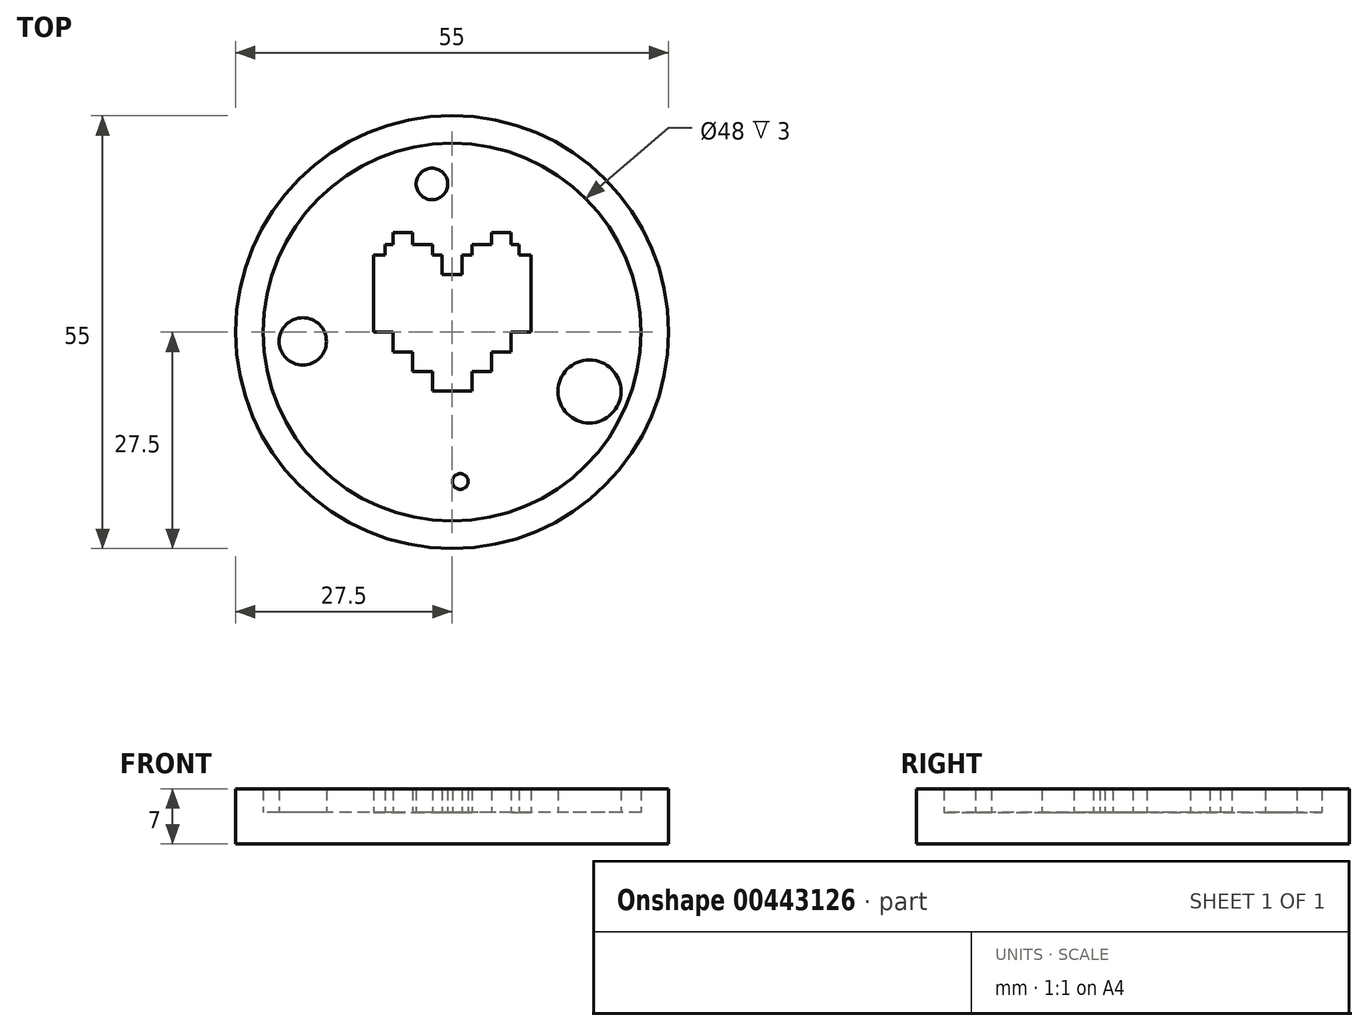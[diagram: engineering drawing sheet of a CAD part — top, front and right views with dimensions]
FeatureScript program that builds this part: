
annotation { "Feature Type Name" : "Feature", "Feature Type Description" : "" }
export const myFeature = defineFeature(function(context is Context, id is Id, definition is map)
    precondition{}
    {
        {
            var Q0;
            Q0=qCreatedBy(makeId("Top.planeOp"),FACE);
            var sketch = newSketch(context, id + "F0", { "sketchPlane" : qUnion([Q0])});
            skCircle(sketch, "E0", {"center": v(0, 0) * mm, "radius": 27.5 * mm});
            skCircle(sketch, "E1", {"center": v(0, 0) * mm, "radius": 24 * mm});
            skSolve(sketch);
        }
        {
            var Q0;
            Q0=makeQuery(id+"F0.imprint","IMPRINT",FACE,{"disambiguationData":[TD([[makeQuery(id+"F0.imprint","IMPRINT",EDGE,{"derivedFrom":sQuery(id+"F0.wireOp",EDGE,"E0")}),1.0]])]});
            extrude(context, id + "F1", {"entities" : qUnion([Q0]), "depth" : 7 * mm});
        }
        {
            var Q0;
            Q0=qCreatedBy(makeId("Top.planeOp"),FACE);
            var sketch = newSketch(context, id + "F2", { "sketchPlane" : qUnion([Q0])});
            skCircle(sketch, "E2", {"center": v(0, 0) * mm, "radius": 27.5 * mm});
            skSolve(sketch);
        }
        {
            var Q0;
            Q0 = qSketchRegion(id + "F2", true);
            extrude(context, id + "F3", {"entities" : qUnion([Q0]), "operationType" : NewBodyOperationType.ADD, "depth" : 4 * mm});
        }
        {
            var Q0;
            Q0=makeQuery(id+"F3.opExtrude","CAP_FACE",FACE,{"disambiguationData":[OSD([sQuery(id+"F2.wireOp",EDGE,"E2")])],"isStart":false});
            var sketch = newSketch(context, id + "F4", { "sketchPlane" : qUnion([Q0])});
            skCircle(sketch, "E3", {"center": v(-18.96, -1.17) * mm, "radius": 3 * mm});
            skCircle(sketch, "E4", {"center": v(1.04, -18.97) * mm, "radius": 1 * mm});
            skCircle(sketch, "E5", {"center": v(17.44, -7.53) * mm, "radius": 4 * mm});
            skCircle(sketch, "E6", {"center": v(-2.56, 18.83) * mm, "radius": 2 * mm});
            skSolve(sketch);
        }
        {
            var Q0;
            Q0 = qSketchRegion(id + "F4", true);
            extrude(context, id + "F5", {"entities" : qUnion([Q0]), "operationType" : NewBodyOperationType.ADD, "depth" : 3 * mm});
        }
        {
            var Q0;
            Q0=qCreatedBy(makeId("Top.planeOp"),FACE);
            var sketch = newSketch(context, id + "F6", { "sketchPlane" : qUnion([Q0])});
            skLineSegment(sketch, "E7", {"start": v(0, -7.5) * mm, "end": v(2.5, -7.5) * mm});
            skLineSegment(sketch, "E8", {"start": v(2.5, -7.5) * mm, "end": v(2.5, -5) * mm});
            skLineSegment(sketch, "E9", {"start": v(2.5, -5) * mm, "end": v(5, -5) * mm});
            skLineSegment(sketch, "E10", {"start": v(5, -5) * mm, "end": v(5, -2.5) * mm});
            skLineSegment(sketch, "E11", {"start": v(5, -2.5) * mm, "end": v(7.5, -2.5) * mm});
            skLineSegment(sketch, "E12", {"start": v(7.5, -2.5) * mm, "end": v(7.5, 0) * mm});
            skLineSegment(sketch, "E13", {"start": v(7.5, 0) * mm, "end": v(10, 0) * mm});
            skLineSegment(sketch, "E14", {"start": v(10, 0) * mm, "end": v(10, 9.8) * mm});
            skLineSegment(sketch, "E15", {"start": v(10, 9.8) * mm, "end": v(8.5, 9.8) * mm});
            skLineSegment(sketch, "E16", {"start": v(8.5, 9.8) * mm, "end": v(8.5, 11.12) * mm});
            skLineSegment(sketch, "E17", {"start": v(8.5, 11.12) * mm, "end": v(7.5, 11.12) * mm});
            skLineSegment(sketch, "E18", {"start": v(7.5, 11.12) * mm, "end": v(7.5, 12.62) * mm});
            skLineSegment(sketch, "E19", {"start": v(7.5, 12.62) * mm, "end": v(5, 12.62) * mm});
            skLineSegment(sketch, "E20", {"start": v(5, 12.62) * mm, "end": v(5, 11.12) * mm});
            skLineSegment(sketch, "E21", {"start": v(5, 11.12) * mm, "end": v(2.5, 11.12) * mm});
            skLineSegment(sketch, "E22", {"start": v(2.5, 11.12) * mm, "end": v(2.5, 9.8) * mm});
            skLineSegment(sketch, "E23", {"start": v(2.5, 9.8) * mm, "end": v(1.25, 9.8) * mm});
            skLineSegment(sketch, "E24", {"start": v(1.25, 9.8) * mm, "end": v(1.25, 7.3) * mm});
            skLineSegment(sketch, "E25", {"start": v(1.25, 7.3) * mm, "end": v(0, 7.3) * mm});
            skLineSegment(sketch, "E26.MirrorCS", {"start": v(-10, 9.8) * mm, "end": v(-8.5, 9.8) * mm});
            skLineSegment(sketch, "E27.MirrorCS", {"start": v(-8.5, 9.8) * mm, "end": v(-8.5, 11.12) * mm});
            skLineSegment(sketch, "E28.MirrorCS", {"start": v(-2.5, 9.8) * mm, "end": v(-1.25, 9.8) * mm});
            skLineSegment(sketch, "E29.MirrorCS", {"start": v(-2.5, -5) * mm, "end": v(-5, -5) * mm});
            skLineSegment(sketch, "E30.MirrorCS", {"start": v(-2.5, -7.5) * mm, "end": v(-2.5, -5) * mm});
            skLineSegment(sketch, "E31.MirrorCS", {"start": v(-5, 11.12) * mm, "end": v(-2.5, 11.12) * mm});
            skLineSegment(sketch, "E32.MirrorCS", {"start": v(-5, 12.62) * mm, "end": v(-5, 11.12) * mm});
            skLineSegment(sketch, "E33.MirrorCS", {"start": v(-7.5, 11.12) * mm, "end": v(-7.5, 12.62) * mm});
            skLineSegment(sketch, "E34.MirrorCS", {"start": v(-8.5, 11.12) * mm, "end": v(-7.5, 11.12) * mm});
            skLineSegment(sketch, "E35.MirrorCS", {"start": v(-2.5, 11.12) * mm, "end": v(-2.5, 9.8) * mm});
            skLineSegment(sketch, "E36.MirrorCS", {"start": v(-1.25, 7.3) * mm, "end": v(0, 7.3) * mm});
            skLineSegment(sketch, "E37.MirrorCS", {"start": v(-1.25, 9.8) * mm, "end": v(-1.25, 7.3) * mm});
            skLineSegment(sketch, "E38.MirrorCS", {"start": v(-10, 0) * mm, "end": v(-10, 9.8) * mm});
            skLineSegment(sketch, "E39.MirrorCS", {"start": v(-7.5, 0) * mm, "end": v(-10, 0) * mm});
            skLineSegment(sketch, "E40.MirrorCS", {"start": v(-7.5, -2.5) * mm, "end": v(-7.5, 0) * mm});
            skLineSegment(sketch, "E41.MirrorCS", {"start": v(-7.5, 12.62) * mm, "end": v(-5, 12.62) * mm});
            skLineSegment(sketch, "E42.MirrorCS", {"start": v(-5, -5) * mm, "end": v(-5, -2.5) * mm});
            skLineSegment(sketch, "E43.MirrorCS", {"start": v(-5, -2.5) * mm, "end": v(-7.5, -2.5) * mm});
            skLineSegment(sketch, "E44.MirrorCS", {"start": v(0, -7.5) * mm, "end": v(-2.5, -7.5) * mm});
            skSolve(sketch);
        }
        {
            var Q0;
            Q0 = qSketchRegion(id + "F6", true);
            extrude(context, id + "F7", {"entities" : qUnion([Q0]), "operationType" : NewBodyOperationType.ADD, "depth" : 7 * mm});
        }
    });
